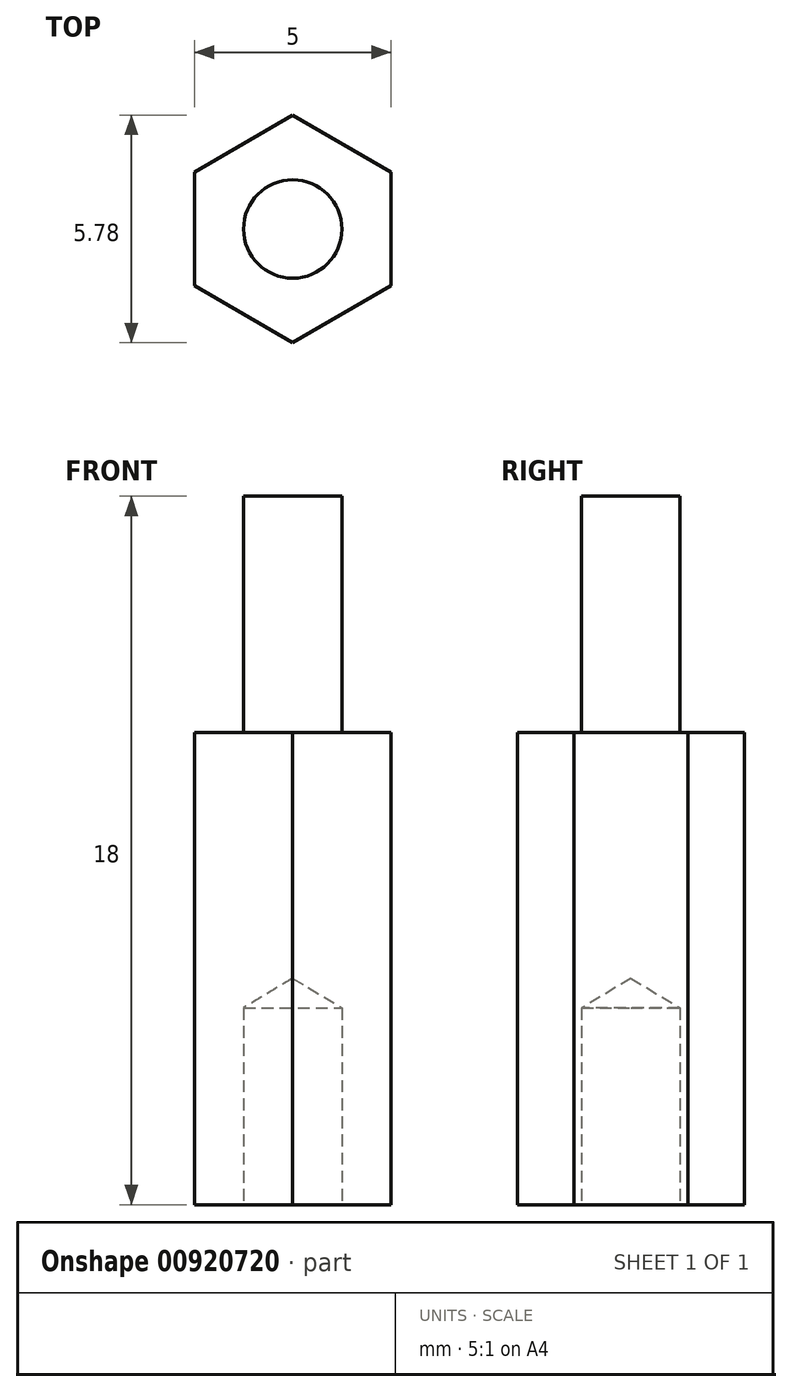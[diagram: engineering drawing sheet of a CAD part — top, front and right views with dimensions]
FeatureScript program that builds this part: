
annotation { "Feature Type Name" : "Feature", "Feature Type Description" : "" }
export const myFeature = defineFeature(function(context is Context, id is Id, definition is map)
    precondition{}
    {
        {
            var Q0;
            Q0=qCreatedBy(makeId("Top.planeOp"),FACE);
            var sketch = newSketch(context, id + "F0", { "sketchPlane" : qUnion([Q0])});
            skCircle(sketch, "E0.cCircle", {"center": v(0, 0) * mm, "radius": 2.5 * mm, "construction": true});
            skLineSegment(sketch, "E0.0", {"start": v(0, 2.89) * mm, "end": v(2.5, 1.44) * mm});
            skLineSegment(sketch, "E0.1", {"start": v(2.5, 1.44) * mm, "end": v(2.5, -1.44) * mm});
            skLineSegment(sketch, "E0.2", {"start": v(2.5, -1.44) * mm, "end": v(0, -2.89) * mm});
            skLineSegment(sketch, "E0.3", {"start": v(0, -2.89) * mm, "end": v(-2.5, -1.44) * mm});
            skLineSegment(sketch, "E0.4", {"start": v(-2.5, -1.44) * mm, "end": v(-2.5, 1.44) * mm});
            skLineSegment(sketch, "E0.5", {"start": v(-2.5, 1.44) * mm, "end": v(0, 2.89) * mm});
            skPoint(sketch, "E0.0.midPoint", {"position": v(1.25, 2.17) * mm});
            skSolve(sketch);
        }
        {
            var Q0;
            Q0 = qSketchRegion(id + "F0", true);
            extrude(context, id + "F1", {"entities" : qUnion([Q0]), "depth" : 12 * mm, "offsetDistance" : 25 * mm});
        }
        {
            var Q0;
            Q0=makeQuery(id+"F1.opExtrude","CAP_FACE",FACE,{"disambiguationData":[OSD([sQuery(id+"F0.wireOp",EDGE,"E0.0"),sQuery(id+"F0.wireOp",EDGE,"E0.1"),sQuery(id+"F0.wireOp",EDGE,"E0.2"),sQuery(id+"F0.wireOp",EDGE,"E0.3"),sQuery(id+"F0.wireOp",EDGE,"E0.4"),sQuery(id+"F0.wireOp",EDGE,"E0.5")])],"isStart":false});
            var sketch = newSketch(context, id + "F2", { "sketchPlane" : qUnion([Q0])});
            skCircle(sketch, "E1", {"center": v(0, 0) * mm, "radius": 1.25 * mm});
            skSolve(sketch);
        }
        {
            var Q0;
            Q0 = qSketchRegion(id + "F2", true);
            extrude(context, id + "F3", {"entities" : qUnion([Q0]), "operationType" : NewBodyOperationType.ADD, "depth" : 6 * mm, "offsetDistance" : 25 * mm});
        }
        {
            var Q0;
            Q0=makeQuery(id+"F1.opExtrude","CAP_FACE",FACE,{"disambiguationData":[OSD([sQuery(id+"F0.wireOp",EDGE,"E0.0"),sQuery(id+"F0.wireOp",EDGE,"E0.1"),sQuery(id+"F0.wireOp",EDGE,"E0.2"),sQuery(id+"F0.wireOp",EDGE,"E0.3"),sQuery(id+"F0.wireOp",EDGE,"E0.4"),sQuery(id+"F0.wireOp",EDGE,"E0.5")])],"isStart":true});
            var sketch = newSketch(context, id + "F4", { "sketchPlane" : qUnion([Q0])});
            skPoint(sketch, "E2", {"position": v(0, 0) * mm});
            skSolve(sketch);
        }
        {
            var Q0;
            Q0=sQuery(id+"F4.wireOp",VERTEX,"E2");
            var Q1;
            Q1=makeQuery(id+"F1.opExtrude","SWEPT_BODY",BODY,{"disambiguationData":[OSD([sQuery(id+"F0.wireOp",EDGE,"E0.0"),sQuery(id+"F0.wireOp",EDGE,"E0.1"),sQuery(id+"F0.wireOp",EDGE,"E0.2"),sQuery(id+"F0.wireOp",EDGE,"E0.3"),sQuery(id+"F0.wireOp",EDGE,"E0.4"),sQuery(id+"F0.wireOp",EDGE,"E0.5")])]});
            hole(context, id + "F5", {"style" : HoleStyle.SIMPLE, "endStyle" : HoleEndStyle.BLIND, "holeDiameter" : 2.5 * mm, "majorDiameter" : 5 * mm, "holeDepth" : 5 * mm, "isTappedThrough" : true, "tappedDepth" : 12 * mm, "tapClearance" : 3, "locations" : qUnion([Q0]), "scope" : qUnion([Q1])});
        }
    });
